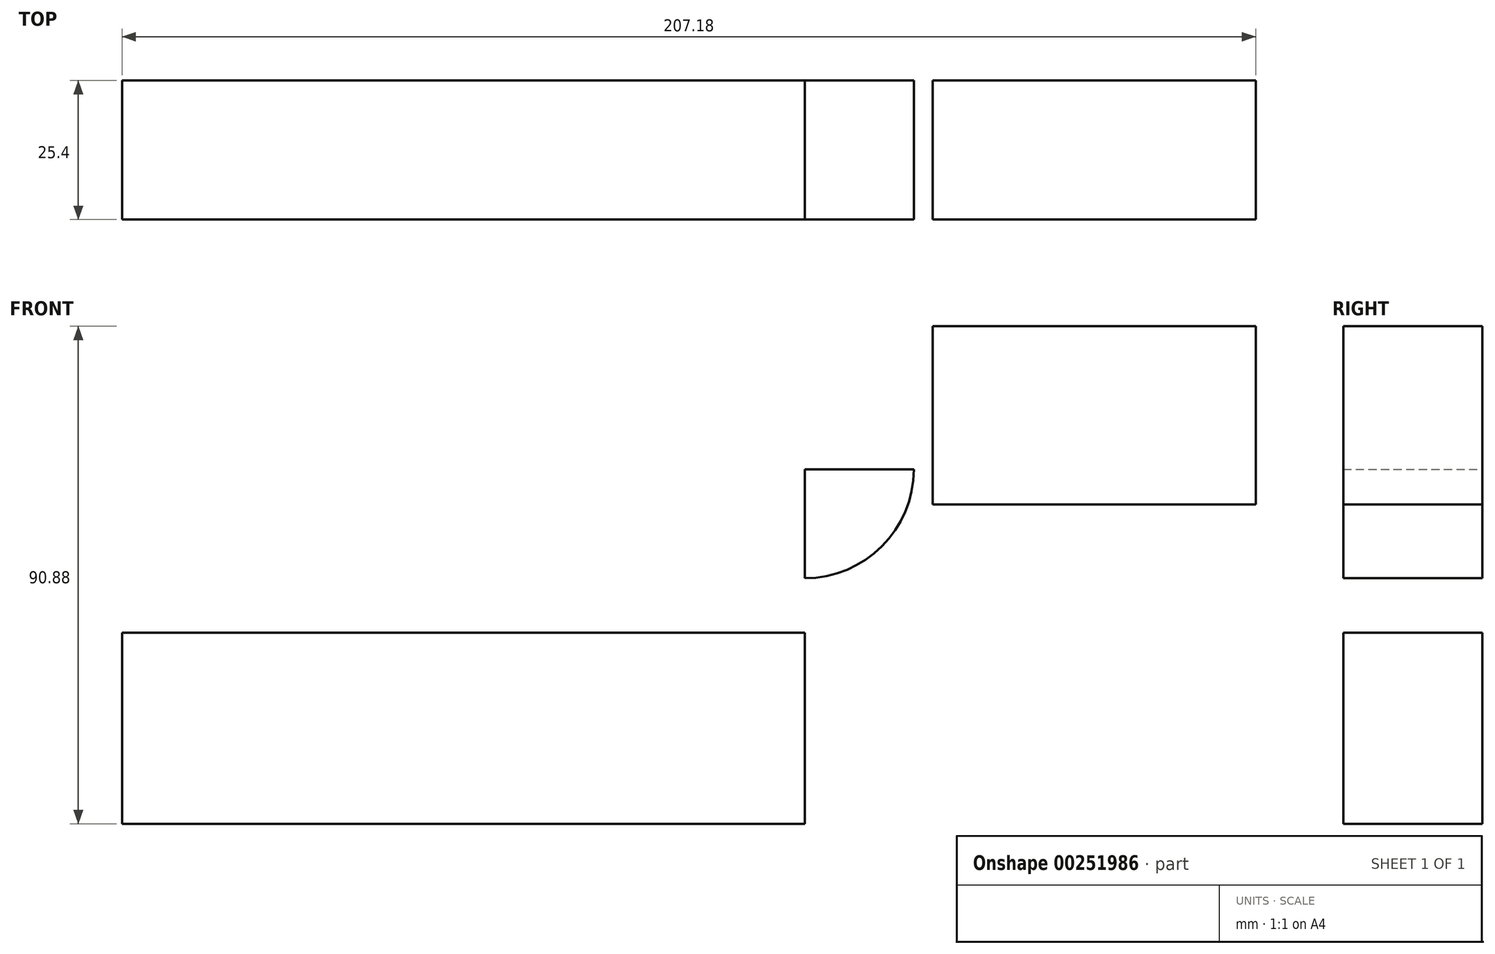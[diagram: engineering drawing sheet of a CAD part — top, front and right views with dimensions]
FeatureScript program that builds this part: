
annotation { "Feature Type Name" : "Feature", "Feature Type Description" : "" }
export const myFeature = defineFeature(function(context is Context, id is Id, definition is map)
    precondition{}
    {
        {
            var Q0;
            Q0=qCreatedBy(makeId("Front.planeOp"),FACE);
            var sketch = newSketch(context, id + "F0", { "sketchPlane" : qUnion([Q0])});
            skLineSegment(sketch, "E0.bottom", {"start": v(-59, 18.82) * mm, "end": v(65.78, 18.82) * mm});
            skLineSegment(sketch, "E0.top", {"start": v(-59, -16.1) * mm, "end": v(65.78, -16.1) * mm});
            skLineSegment(sketch, "E0.left", {"start": v(-59, 18.82) * mm, "end": v(-59, -16.1) * mm});
            skLineSegment(sketch, "E0.right", {"start": v(65.78, 18.82) * mm, "end": v(65.78, -16.1) * mm});
            skLineSegment(sketch, "E1.bottom", {"start": v(89.18, 74.77) * mm, "end": v(148.18, 74.77) * mm});
            skLineSegment(sketch, "E1.top", {"start": v(89.18, 42.22) * mm, "end": v(148.18, 42.22) * mm});
            skLineSegment(sketch, "E1.left", {"start": v(89.18, 74.77) * mm, "end": v(89.18, 42.22) * mm});
            skLineSegment(sketch, "E1.right", {"start": v(148.18, 74.77) * mm, "end": v(148.18, 42.22) * mm});
            skLineSegment(sketch, "E2", {"start": v(65.78, 18.82) * mm, "end": v(65.78, 48.66) * mm});
            skArc(sketch, "E3", {"start": v(79.35, 63.24) * mm, "mid": v(73.74, 30.4) * mm, "end": v(45.87, 48.66) * mm});
            skLineSegment(sketch, "E4", {"start": v(65.78, 48.66) * mm, "end": v(130.89, 48.66) * mm});
            skSolve(sketch);
        }
        {
            var Q0;
            Q0 = qSketchRegion(id + "F0", true);
            extrude(context, id + "F1", {"entities" : qUnion([Q0]), "depth" : 25.4 * mm});
        }
    });
